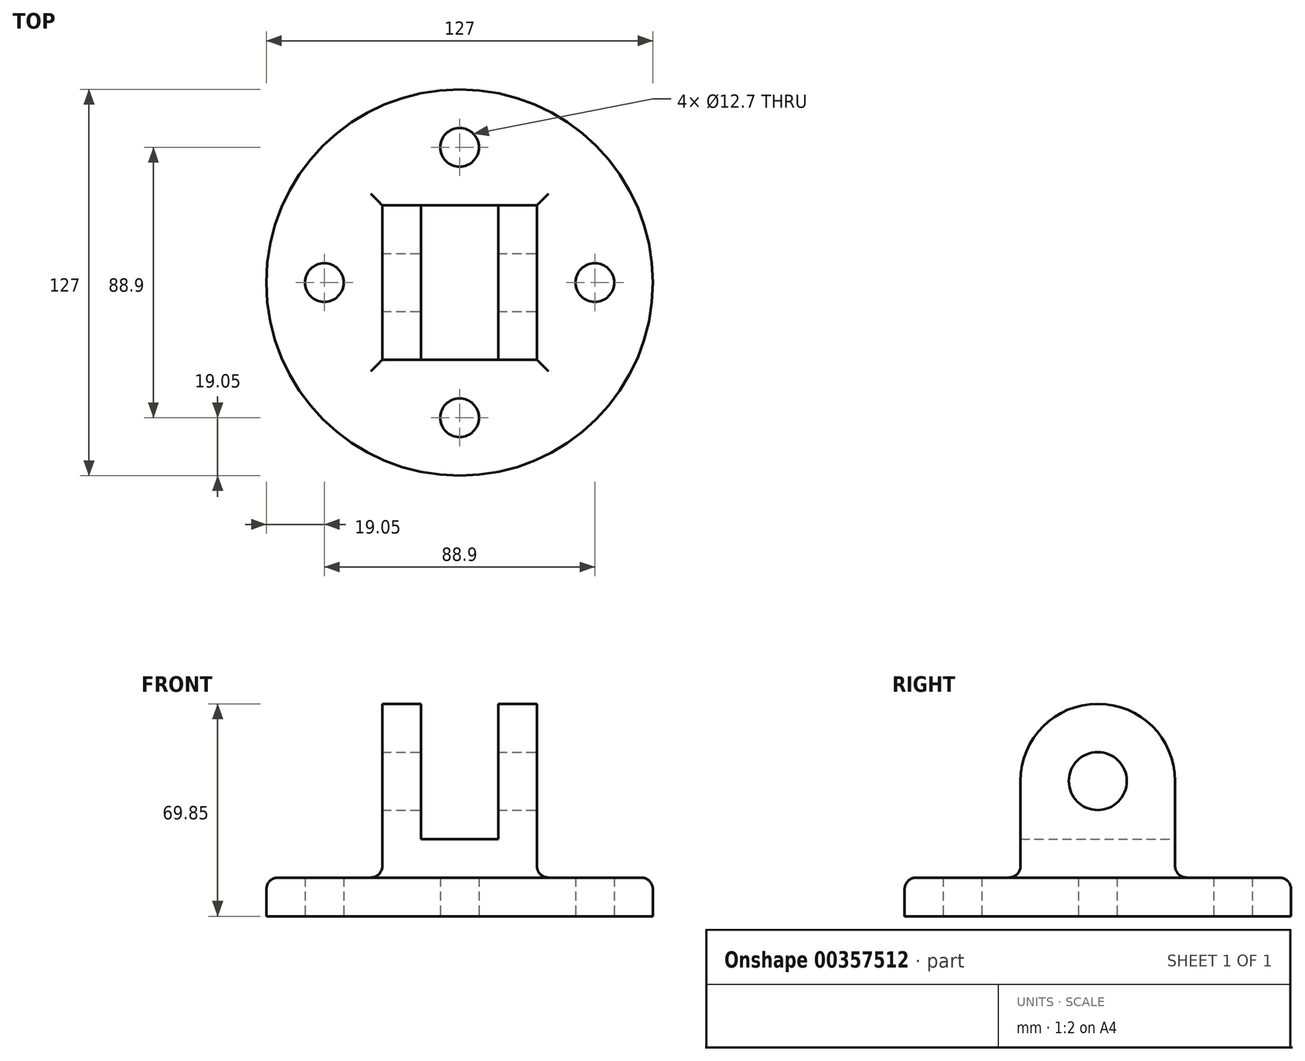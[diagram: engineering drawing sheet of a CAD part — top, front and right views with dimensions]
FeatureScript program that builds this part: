
annotation { "Feature Type Name" : "Feature", "Feature Type Description" : "" }
export const myFeature = defineFeature(function(context is Context, id is Id, definition is map)
    precondition{}
    {
        {
            var Q0;
            Q0=qCreatedBy(makeId("Top.planeOp"),FACE);
            var sketch = newSketch(context, id + "F0", { "sketchPlane" : qUnion([Q0])});
            skCircle(sketch, "E0", {"center": v(0, 0) * mm, "radius": 63.5 * mm});
            skCircle(sketch, "E1", {"center": v(0, 44.45) * mm, "radius": 6.35 * mm});
            skCircle(sketch, "E2", {"center": v(-44.45, 0) * mm, "radius": 6.35 * mm});
            skCircle(sketch, "E3", {"center": v(0, -44.45) * mm, "radius": 6.35 * mm});
            skCircle(sketch, "E4", {"center": v(44.45, 0) * mm, "radius": 6.35 * mm});
            skCircle(sketch, "E5", {"center": v(0, 0) * mm, "radius": 44.45 * mm, "construction": true});
            skSolve(sketch);
        }
        {
            var Q0;
            Q0 = qSketchRegion(id + "F0", true);
            extrude(context, id + "F1", {"entities" : qUnion([Q0]), "depth" : 12.7 * mm});
        }
        {
            var Q0;
            Q0=qCreatedBy(makeId("Front.planeOp"),FACE);
            var sketch = newSketch(context, id + "F2", { "sketchPlane" : qUnion([Q0])});
            skLineSegment(sketch, "E6", {"start": v(-25.4, 0) * mm, "end": v(-25.4, 76.2) * mm});
            skLineSegment(sketch, "E7", {"start": v(-25.4, 76.2) * mm, "end": v(-12.7, 76.2) * mm});
            skLineSegment(sketch, "E8", {"start": v(-12.7, 76.2) * mm, "end": v(-12.7, 25.4) * mm});
            skLineSegment(sketch, "E9", {"start": v(-12.7, 25.4) * mm, "end": v(12.7, 25.4) * mm});
            skLineSegment(sketch, "E10", {"start": v(12.7, 25.4) * mm, "end": v(12.7, 76.2) * mm});
            skLineSegment(sketch, "E11", {"start": v(12.7, 76.2) * mm, "end": v(25.4, 76.2) * mm});
            skLineSegment(sketch, "E12", {"start": v(25.4, 76.2) * mm, "end": v(25.4, 0) * mm});
            skLineSegment(sketch, "E13", {"start": v(-25.4, 0) * mm, "end": v(25.4, 0) * mm});
            skSolve(sketch);
        }
        {
            var Q0;
            Q0 = qSketchRegion(id + "F2", true);
            extrude(context, id + "F3", {"entities" : qUnion([Q0]), "operationType" : NewBodyOperationType.ADD, "endBound" : BoundingType.SYMMETRIC, "depth" : 50.8 * mm});
        }
        {
            var Q0;
            Q0=makeQuery(id+"F3.opExtrude","SWEPT_FACE",FACE,{"disambiguationData":[OSD([sQuery(id+"F2.wireOp",EDGE,"E12")])]});
            var sketch = newSketch(context, id + "F4", { "sketchPlane" : qUnion([Q0])});
            skCircle(sketch, "E14", {"center": v(0, 44.45) * mm, "radius": 9.53 * mm});
            skPoint(sketch, "E14.centerSnap0", {"position": v(-25.4, 44.45) * mm});
            skArc(sketch, "E15", {"start": v(25.4, 44.45) * mm, "mid": v(0, 69.85) * mm, "end": v(-25.4, 44.45) * mm});
            skSolve(sketch);
        }
        {
            var Q0;
            {var subQ0=sQuery(id+"F4.wireOp",EDGE,"E15");Q0=makeQuery(id+"F4.imprint","IMPRINT",FACE,{"disambiguationData":[TD([[makeQuery(id+"F4.imprint","IMPRINT",EDGE,{"derivedFrom":subQ0}),-1.0]])]});}
            extrude(context, id + "F5", {"entities" : qUnion([Q0]), "operationType" : NewBodyOperationType.REMOVE, "endBound" : BoundingType.THROUGH_ALL, "oppositeDirection" : true, "depth" : 25.4 * mm});
        }
        {
            var Q0;
            Q0=makeQuery(id+"F4.imprint","IMPRINT",FACE,{"disambiguationData":[TD([[makeQuery(id+"F4.imprint","IMPRINT",EDGE,{"derivedFrom":sQuery(id+"F4.wireOp",EDGE,"E14")}),1.0]])]});
            extrude(context, id + "F6", {"entities" : qUnion([Q0]), "operationType" : NewBodyOperationType.REMOVE, "endBound" : BoundingType.THROUGH_ALL, "oppositeDirection" : true, "depth" : 25.4 * mm});
        }
        {
            var Q0;
            Q0=makeQuery(id+"F1.opExtrude","CAP_EDGE",EDGE,{"disambiguationData":[OSD([sQuery(id+"F0.wireOp",EDGE,"E0")])],"isStart":false});
            var Q1;
            Q1=makeQuery(id+"F3.boolean.opBoolean","INTERSECT",EDGE,{"derivedFrom":[makeQuery(id+"F1.opExtrude","CAP_FACE",FACE,{"disambiguationData":[OSD([sQuery(id+"F0.wireOp",EDGE,"E0"),sQuery(id+"F0.wireOp",EDGE,"E1"),sQuery(id+"F0.wireOp",EDGE,"E2"),sQuery(id+"F0.wireOp",EDGE,"E3"),sQuery(id+"F0.wireOp",EDGE,"E4")])],"isStart":false}),makeQuery(id+"F3.opExtrude","SWEPT_FACE",FACE,{"disambiguationData":[OSD([sQuery(id+"F2.wireOp",EDGE,"E12")])]})]});
            var Q2;
            Q2=makeQuery(id+"F3.boolean.opBoolean","INTERSECT",EDGE,{"derivedFrom":[makeQuery(id+"F1.opExtrude","CAP_FACE",FACE,{"disambiguationData":[OSD([sQuery(id+"F0.wireOp",EDGE,"E0"),sQuery(id+"F0.wireOp",EDGE,"E1"),sQuery(id+"F0.wireOp",EDGE,"E2"),sQuery(id+"F0.wireOp",EDGE,"E3"),sQuery(id+"F0.wireOp",EDGE,"E4")])],"isStart":false}),makeQuery(id+"F3.opExtrude","CAP_FACE",FACE,{"disambiguationData":[OSD([sQuery(id+"F2.wireOp",EDGE,"E6"),sQuery(id+"F2.wireOp",EDGE,"E7"),sQuery(id+"F2.wireOp",EDGE,"E8"),sQuery(id+"F2.wireOp",EDGE,"E9"),sQuery(id+"F2.wireOp",EDGE,"E10"),sQuery(id+"F2.wireOp",EDGE,"E11"),sQuery(id+"F2.wireOp",EDGE,"E12"),sQuery(id+"F2.wireOp",EDGE,"E13")])],"isStart":false})]});
            var Q3;
            Q3=makeQuery(id+"F3.boolean.opBoolean","INTERSECT",EDGE,{"derivedFrom":[makeQuery(id+"F1.opExtrude","CAP_FACE",FACE,{"disambiguationData":[OSD([sQuery(id+"F0.wireOp",EDGE,"E0"),sQuery(id+"F0.wireOp",EDGE,"E1"),sQuery(id+"F0.wireOp",EDGE,"E2"),sQuery(id+"F0.wireOp",EDGE,"E3"),sQuery(id+"F0.wireOp",EDGE,"E4")])],"isStart":false}),makeQuery(id+"F3.opExtrude","CAP_FACE",FACE,{"disambiguationData":[OSD([sQuery(id+"F2.wireOp",EDGE,"E6"),sQuery(id+"F2.wireOp",EDGE,"E7"),sQuery(id+"F2.wireOp",EDGE,"E8"),sQuery(id+"F2.wireOp",EDGE,"E9"),sQuery(id+"F2.wireOp",EDGE,"E10"),sQuery(id+"F2.wireOp",EDGE,"E11"),sQuery(id+"F2.wireOp",EDGE,"E12"),sQuery(id+"F2.wireOp",EDGE,"E13")])],"isStart":true})]});
            var Q4;
            Q4=makeQuery(id+"F3.boolean.opBoolean","INTERSECT",EDGE,{"derivedFrom":[makeQuery(id+"F1.opExtrude","CAP_FACE",FACE,{"disambiguationData":[OSD([sQuery(id+"F0.wireOp",EDGE,"E0"),sQuery(id+"F0.wireOp",EDGE,"E1"),sQuery(id+"F0.wireOp",EDGE,"E2"),sQuery(id+"F0.wireOp",EDGE,"E3"),sQuery(id+"F0.wireOp",EDGE,"E4")])],"isStart":false}),makeQuery(id+"F3.opExtrude","SWEPT_FACE",FACE,{"disambiguationData":[OSD([sQuery(id+"F2.wireOp",EDGE,"E6")])]})]});
            fillet(context, id + "F7", {"entities" : qUnion([Q0, Q1, Q2, Q3, Q4]), "radius" : 3.8 * mm, "tangentPropagation" : true, "allowEdgeOverflow" : false});
        }
    });
